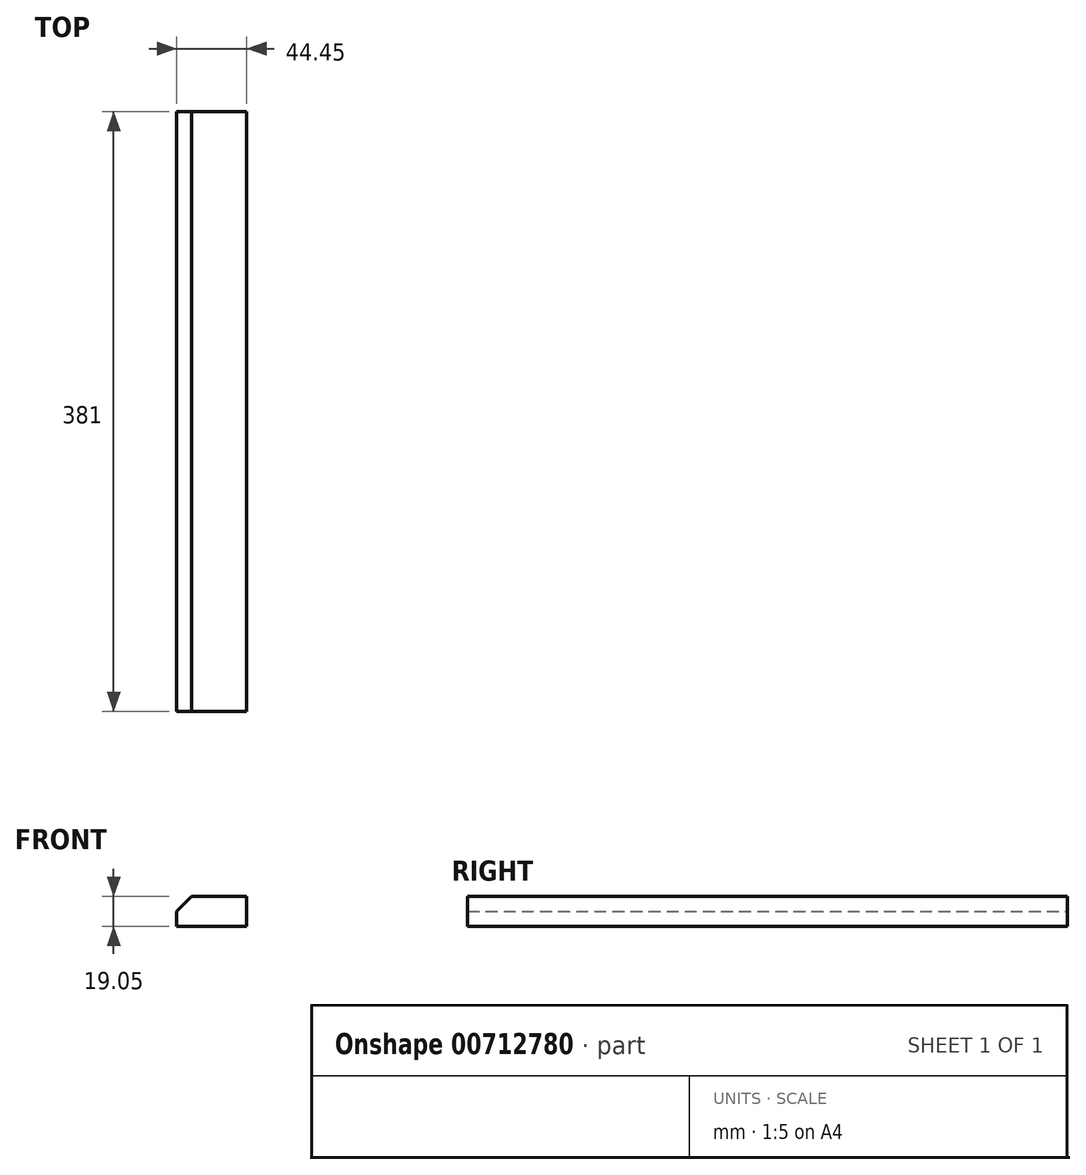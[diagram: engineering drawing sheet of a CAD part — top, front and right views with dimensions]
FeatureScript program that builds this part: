
annotation { "Feature Type Name" : "Feature", "Feature Type Description" : "" }
export const myFeature = defineFeature(function(context is Context, id is Id, definition is map)
    precondition{}
    {
        {
            var Q0;
            Q0=qCreatedBy(makeId("Front.planeOp"),FACE);
            var sketch = newSketch(context, id + "F0", { "sketchPlane" : qUnion([Q0])});
            skLineSegment(sketch, "E0.bottom", {"start": v(-44.45, 19.05) * mm, "end": v(0, 19.05) * mm});
            skLineSegment(sketch, "E0.top", {"start": v(-44.45, 0) * mm, "end": v(0, 0) * mm});
            skLineSegment(sketch, "E0.left", {"start": v(-44.45, 19.05) * mm, "end": v(-44.45, 0) * mm});
            skLineSegment(sketch, "E0.right", {"start": v(0, 19.05) * mm, "end": v(0, 0) * mm});
            skSolve(sketch);
        }
        {
            var Q0;
            Q0 = qSketchRegion(id + "F0", true);
            extrude(context, id + "F1", {"entities" : qUnion([Q0]), "depth" : 381 * mm, "offsetDistance" : 25.4 * mm});
        }
        {
            var Q0;
            Q0=makeQuery(id+"F1.opExtrude","SWEPT_EDGE",EDGE,{"disambiguationData":[OSD([sQuery(id+"F0.wireOp",EDGE,"E0.bottom"),sQuery(id+"F0.wireOp",EDGE,"E0.left")])]});
            chamfer(context, id + "F2", {"entities" : qUnion([Q0]), "width" : 9.52 * mm, "tangentPropagation" : true});
        }
    });
